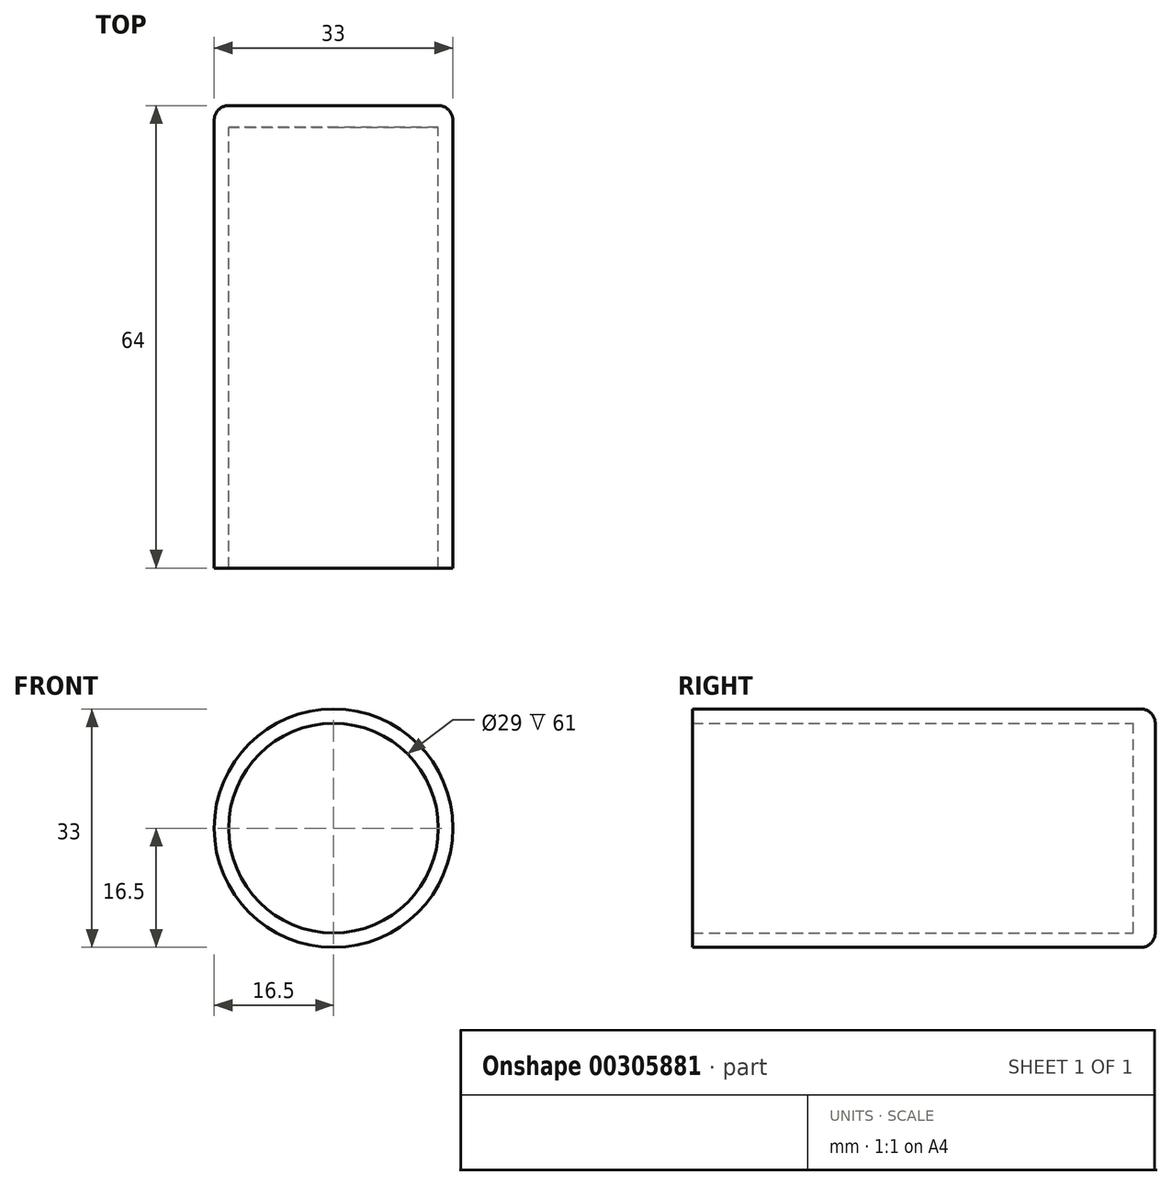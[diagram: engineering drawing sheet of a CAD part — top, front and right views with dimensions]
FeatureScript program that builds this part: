
annotation { "Feature Type Name" : "Feature", "Feature Type Description" : "" }
export const myFeature = defineFeature(function(context is Context, id is Id, definition is map)
    precondition{}
    {
        {
            var Q0;
            Q0=qCreatedBy(makeId("Front.planeOp"),FACE);
            var sketch = newSketch(context, id + "F0", { "sketchPlane" : qUnion([Q0])});
            skCircle(sketch, "E0", {"center": v(0, 0) * mm, "radius": 16.5 * mm});
            skSolve(sketch);
        }
        {
            var Q0;
            Q0 = qSketchRegion(id + "F0", true);
            extrude(context, id + "F1", {"entities" : qUnion([Q0]), "depth" : 3 * mm});
        }
        {
            var Q0;
            Q0=makeQuery(id+"F1.opExtrude","CAP_FACE",FACE,{"disambiguationData":[OSD([sQuery(id+"F0.wireOp",EDGE,"E0")])],"isStart":false});
            var sketch = newSketch(context, id + "F2", { "sketchPlane" : qUnion([Q0])});
            skCircle(sketch, "E1", {"center": v(0, 0) * mm, "radius": 14.5 * mm});
            skSolve(sketch);
        }
        {
            var Q0;
            Q0=makeQuery(id+"F2.imprint","IMPRINT",FACE,{"disambiguationData":[TD([[makeQuery(id+"F2.imprint","IMPRINT",EDGE,{"derivedFrom":sQuery(id+"F2.wireOp",EDGE,"E1")}),-1.0]])]});
            extrude(context, id + "F3", {"entities" : qUnion([Q0]), "operationType" : NewBodyOperationType.ADD, "depth" : 61 * mm});
        }
        {
            var Q0;
            Q0=makeQuery(id+"F1.opExtrude","CAP_EDGE",EDGE,{"disambiguationData":[OSD([sQuery(id+"F0.wireOp",EDGE,"E0")])],"isStart":true});
            fillet(context, id + "F4", {"entities" : qUnion([Q0]), "radius" : 2 * mm, "tangentPropagation" : true, "allowEdgeOverflow" : false});
        }
    });
